# Revit family: Ladder-Precision_Ladders-Fixed_Ladder_w_Parapet_Platform_and_Roof-Side_Return
name_source: partatom
category: Specialty Equipment
revit_build: Autodesk Revit Architecture 2014 (Build: 20131024_2115(x64)
units: mm (PartAtom-declared; Revit-internal decimal feet)

## types (1)
- Fixed Ladder With Parapet Platform & Roofside Return
    Additional Mat Finishes = Polyurethane - Precision Ladders LLC - Safety Cap
    Default Elevation = 0' - 0"
    Description = Fixed Ladder
    Finish = Metal - Precision Ladders LLC - Aluminium
    Manufacturer = Precision Ladders, LLC
    Model = FL-06
    Overall Width = 2' - 2 1/8"
    Product Documentation Link = http://www.precisionladders.com
    Product Name = Fixed Ladder w/ Parapet Platform & Roofside Return
    Product Page URL = http://www.precisionladders.com
    URL = http://www.precisionladders.com
    Width = 2' - 2 7/8"

## geometry (parser evidence)
native form markers: Blend x4, Sweep x5
no freeform markers — native parametric forms only
